# Revit family: CONV_Zero_GnrlPrpseLmnrs_TrapetsPendant
name_source: partatom
category: Lighting Fixtures
revit_build: Autodesk Revit 2015 (Build: 20140606_1530(x64)
units: mm (PartAtom-declared; Revit-internal decimal feet)

## types (16) — shared parameters
AssetType = Fixed
BIMObjectName = CONV_Zero_GnrlPrpseLmnrs_TrapetsPendant
Brand = Zero
Category = Pendant
Collection = Trapets
Color = Black or white
Color Filter = 16777215
Constituents = Wood knob, end (white, black, yellow, ash or grey). Pull to dim switch.
Designer = Note Design Studio
Dimming Lamp Color Temperature Shift = <None>
DurationUnit = Year
Emit Shape Visible in Rendering = No
Emit from Rectangle Length = 82 mm  [stored 0.269029 ft]
ExpiringDate = 07/2018
Features = Plug or terminal block 5x4mm2
Finish = Painted metal
HasProtectiveEarth = No
IP_Code = IP20
IfcExportAs = IfcLightFixtureType
IfcExportType = NOTDEFINED
LensMaterial = Tempered glass
LightFixtureMountingType = Suspended
LightFixturePlacingType = Ceiling
Manufacturer = Zero
ManufacturerName = Zero
ManufacturerURL = https://www.zerolighting.com
Material = Metal and wood
NBSDescription = General purpose luminaires
NBSReference = 90-60-50/405
Name = GnrlPrpseLmnrs_TrapetsPendant
NominalCurrent = 0 A
NominalDiameter = 800 mm  [stored 2.62467 ft]
NominalFrequencyRange = 50 Hz
NominalHeight = 71 mm  [stored 0.23294 ft]
NominalLength = 82 mm  [stored 0.269029 ft]
NominalRadius = 42 mm  [stored 0.137795 ft]
NominalVoltage = 230 V
NominalVoltageCalc = 0 V
NumberOfPoles = 1
PhaseAngle = 0.00°
Shape = Sculptured
Tilt Angle = 90.00°
URL = https://www.zerolighting.com
Uniclass2 = Pr_70_70_49_86
Uniclass2015Description = Suspended luminaires
Uniclass2015Reference = Pr_70_70_48_86
UsageCurrent = 0 A
Version = 1
VersionDate = 04/01/2018
WarrantyDurationUnit = Year
zero-valued in all types: DefaultElevation, ElectricalDeviceNominalPower, MaintenanceFactor, NumberOfSources

## per-type parameters (varying)
| type | ArticleNumber | ConvergoRefNr | Dimming | Emit from Rectangle Width | Model | ModelNumber | ModelType | NominalWidth | Photometric Web File | Size | TotalWattage |
| Trapets T5/25/28W 1400mm Downlight | 8200-1-01 | 0046-1708-0028-SE | None | 1465 mm  [stored 4.80643 ft] | Trapets T5/25/28W 1400mm Downlight | 8200-1-01 | trapets-pendant-1400 | 1465 mm  [stored 4.80643 ft] | Trapets8200-1-28W_IES.IES | 82x1465x71 mm | 28 W |
| Trapets T5/25/50W 1400mm Downlight HFF | 8200-1-01HFF | 0046-1708-0028-SE | Dimmable with DALI, DSI, SwitchDim | 1465 mm  [stored 4.80643 ft] | TrapetsT5/25/50W 1400mm Downlight HFF | 8200-1-01HFF | trapets-pendant-1400 | 1465 mm  [stored 4.80643 ft] | Trapets8200-1-28W_IES.IES | 82x1465x71 mm | 50 W |
| Trapets T5/32/35W 1700mm Downlight | 8200-3-01 | 0046-1708-0029-SE | None | 1765 mm  [stored 5.79068 ft] | Trapets T5/32/35W 1700mm Downlight | 8200-3-01 | trapets-pendant-1700 | 1765 mm  [stored 5.79068 ft] | Trapets8200-3-35W_IES.IES | 82x1765x71 mm | 35 W |
| Trapets T5/32/45W 1700mm Downlight HFF | 8200-3-01HFF | 0046-1708-0029-SE | Dimmable with DALI, DSI, SwitchDim | 1765 mm  [stored 5.79068 ft] | Trapets T5/32/45W 1700mm Downlight HFF | 8200-3-01HFF | trapets-pendant-1700 | 1765 mm  [stored 5.79068 ft] | Trapets8200-3-35W_IES.IES | 82x1765x71 mm | 45 W |
| Trapets LED 1552LM/19W 1400mm Downlight | 8202-1-01 | 0046-1708-0028-SE | None | 1465 mm  [stored 4.80643 ft] | Trapets LED 1552LM/19W 1400mm Downlight | 8202-1-01 | trapets-pendant-1400 | 1465 mm  [stored 4.80643 ft] | Trapets8202-1-Led_IES.IES | 82x1465x71 mm | 19 W |
| Trapets LED 1552LM/19W 1400mm Downlight HFF | 8202-1-01HFF | 0046-1708-0028-SE | Dimmable with DALI, DSI, SwitchDim | 1465 mm  [stored 4.80643 ft] | Trapets LED 1552LM/19W 1400mm Downlight HFF | 8202-1-01HFF | trapets-pendant-1400 | 1465 mm  [stored 4.80643 ft] | Trapets8202-1-Led_IES.IES | 82x1465x71 mm | 19 W |
| Trapets LED 2516LM/33W 1400mm Downlight | 8203-1-01 | 0046-1708-0028-SE | None | 1465 mm  [stored 4.80643 ft] | Trapets LED 2516LM/33W 1400mm Downlight | 8203-1-01 | trapets-pendant-1400 | 1465 mm  [stored 4.80643 ft] | Trapets8203-1-Led_IES.IES | 82x1465x71 mm | 33 W |
| Trapets LED 2516LM/33W 1400mm Downlight HFF | 8203-1-01HFF | 0046-1708-0028-SE | Dimmable with DALI, DSI, SwitchDim | 1465 mm  [stored 4.80643 ft] | Trapets LED 2516LM/33W 1400mm Downlight HFF | 8203-1-01HFF | trapets-pendant-1400 | 1465 mm  [stored 4.80643 ft] | Trapets8203-1-Led_IES.IES | 82x1465x71 mm | 33 W |
| Trapets LED 2081LM/26W 1700mm Downlight | 8202-3-01 | 0046-1708-0029-SE | None | 1765 mm  [stored 5.79068 ft] | Trapets LED LED 2081LM/26W 1700mm Downlight | 8202-3-01 | trapets-pendant-1700 | 1765 mm  [stored 5.79068 ft] | Trapets8202-3-Led_IES.IES | 82x1765x71 mm | 26 W |
| Trapets LED 2081LM/26W 1700mm Downlight HFF | 8202-3-01HFF | 0046-1708-0029-SE | Dimmable with DALI, DSI, SwitchDim | 1765 mm  [stored 5.79068 ft] | Trapets LED 2081LM/26W 1700mm Downlight HFF | 8202-3-01HFF | trapets-pendant-1700 | 1765 mm  [stored 5.79068 ft] | Trapets8202-3-Led_IES.IES | 82x1765x71 mm | 26 W |
| Trapets LED 3220LM/40W 1700mm Downlight | 8203-3-01 | 0046-1708-0029-SE | None | 1765 mm  [stored 5.79068 ft] | Trapets LED 3220LM/40W 1700mm Downlight | 8203-3-01 | trapets-pendant-1700 | 1765 mm  [stored 5.79068 ft] | Trapets8203-3-LED_IES.IES | 82x1765x71 mm | 40 W |
| Trapets LED 3220LM/40W 1700mm Downlight HFF | 8203-3-01HFF | 0046-1708-0029-SE | Dimmable with DALI, DSI, SwitchDim | 1765 mm  [stored 5.79068 ft] | Trapets LED 3220LM/40W 1700mm Downlight HFF | 8203-3-01HFF | trapets-pendant-1700 | 1765 mm  [stored 5.79068 ft] | Trapets8203-3-LED_IES.IES | 82x1765x71 mm | 40 W |
| Trapets T5/25/28W 1400mm Down & uplight | 8201-1-01 | 0046-1708-0028-SE | None | 1465 mm  [stored 4.80643 ft] | Trapets T5/25/28W 1400mm Down & uplight | 8201-1-01 | trapets-pendant-1400 | 1465 mm  [stored 4.80643 ft] | Trapets8201-1-28W_IES.IES | 82x1465x71 mm | 19 W |
| Trapets T5/25/50W 1400mm Down & uplight HFF | 8201-1-01HFF | 0046-1708-0028-SE | Dimmable with DALI, DSI, SwitchDim | 1465 mm  [stored 4.80643 ft] | Trapets T5/25/50W 1400mm Down & uplight HFF | 8201-1-01HFF | trapets-pendant-1400 | 1465 mm  [stored 4.80643 ft] | Trapets8201-3-49W_IES.IES | 82x1465x71 mm | 50 W |
| Trapets T5/32/35W 1700mm Down & uplight | 8201-3-01 | 0046-1708-0029-SE | None | 1765 mm  [stored 5.79068 ft] | Trapets T5/32/35W 1700mm Down & uplight | 8201-3-01 | trapets-pendant-1700 | 1765 mm  [stored 5.79068 ft] | Trapets8201-3-35W_IES.IES | 82x1765x71 mm | 35 W |
| Trapets T5/32/45W 1700mm Down & uplight HFF | 8201-3-01HFF | 0046-1708-0029-SE | Dimmable with DALI, DSI, SwitchDim | 1765 mm  [stored 5.79068 ft] | Trapets T5/32/45W 1700mm Down & uplight HFF | 8201-3-01HFF | trapets-pendant-1700 | 1765 mm  [stored 5.79068 ft] | Trapets8201-3-49W_IES.IES | 82x1765x71 mm | 35 W |

note: [stored X ft] marks values corroborated as IEEE doubles in the binary element streams (Revit-internal decimal feet)

## geometry (parser evidence)
native form markers: Sweep x8
no freeform markers — native parametric forms only
